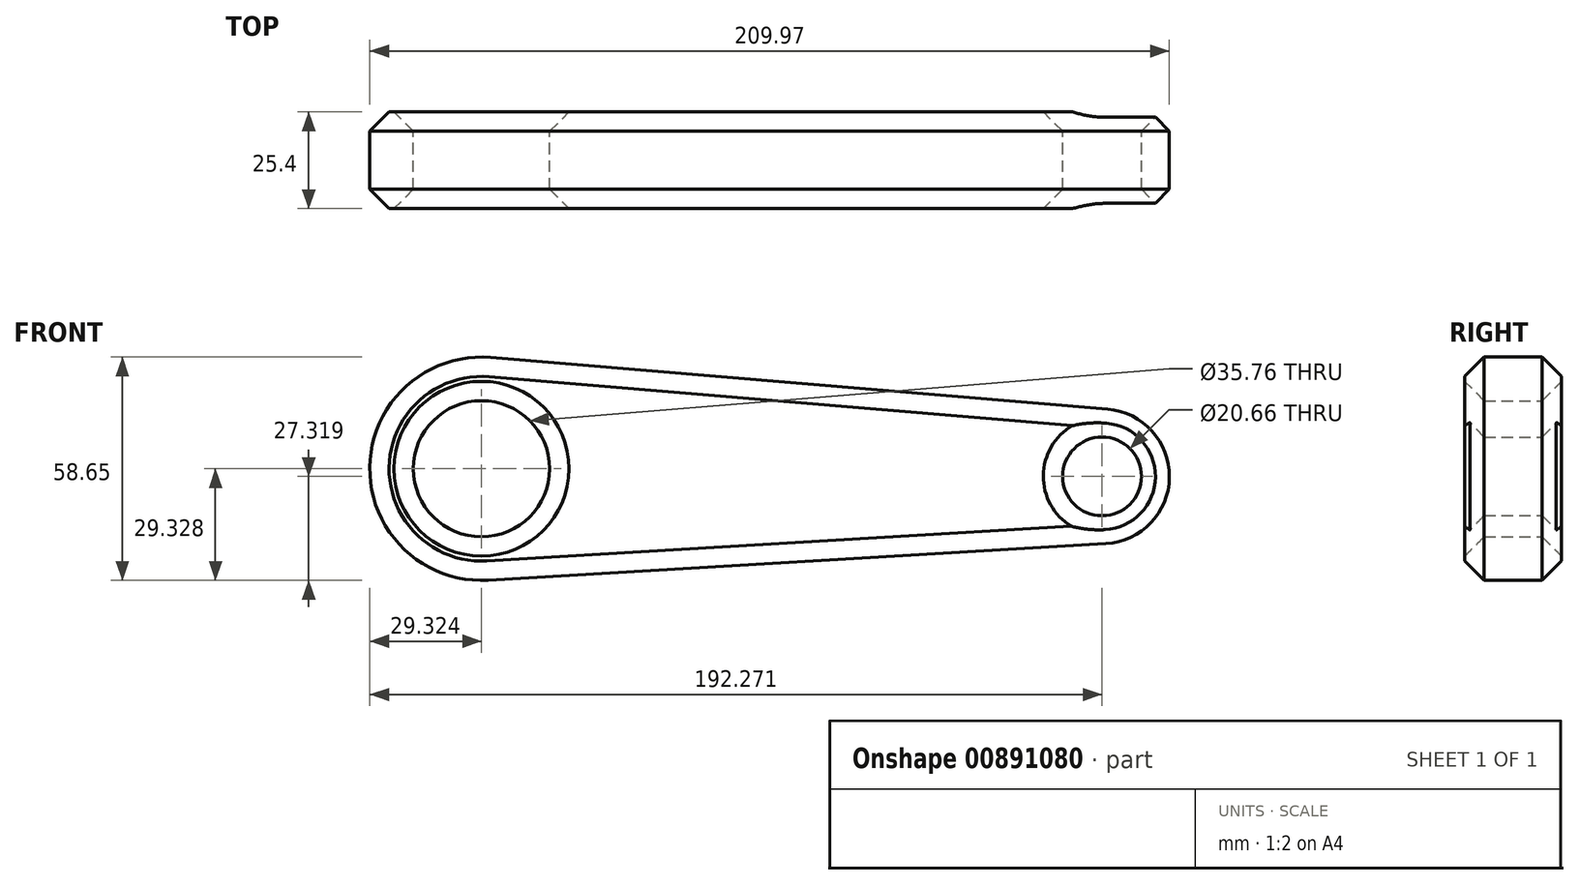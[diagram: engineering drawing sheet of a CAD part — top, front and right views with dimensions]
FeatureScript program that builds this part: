
annotation { "Feature Type Name" : "Feature", "Feature Type Description" : "" }
export const myFeature = defineFeature(function(context is Context, id is Id, definition is map)
    precondition{}
    {
        {
            var Q0;
            Q0=qCreatedBy(makeId("Front.planeOp"),FACE);
            var sketch = newSketch(context, id + "F0", { "sketchPlane" : qUnion([Q0])});
            skCircle(sketch, "E0", {"center": v(-130.06, 19.3) * mm, "radius": 29.33 * mm});
            skCircle(sketch, "E1", {"center": v(32.9, 17.3) * mm, "radius": 17.7 * mm});
            skLineSegment(sketch, "E2", {"start": v(-127.6, 48.53) * mm, "end": v(34.37, 34.94) * mm});
            skLineSegment(sketch, "E3", {"start": v(-128.32, -9.97) * mm, "end": v(33.94, -0.37) * mm});
            skCircle(sketch, "E4", {"center": v(-130.06, 19.3) * mm, "radius": 17.88 * mm});
            skCircle(sketch, "E5", {"center": v(32.9, 17.3) * mm, "radius": 10.33 * mm});
            skSolve(sketch);
        }
        {
            var Q0;
            Q0 = qSketchRegion(id + "F0", true);
            extrude(context, id + "F1", {"entities" : qUnion([Q0]), "depth" : 25.4 * mm, "offsetDistance" : 25.4 * mm});
        }
        {
            var Q0;
            Q0=makeQuery(id+"F1.opExtrude","CAP_EDGE",EDGE,{"disambiguationData":[OSD([sQuery(id+"F0.wireOp",EDGE,"E2")])],"isStart":false});
            var Q1;
            Q1=makeQuery(id+"F1.opExtrude","CAP_EDGE",EDGE,{"disambiguationData":[OSD([sQuery(id+"F0.wireOp",EDGE,"E0")])],"isStart":false});
            var Q2;
            Q2=makeQuery(id+"F1.opExtrude","CAP_EDGE",EDGE,{"disambiguationData":[OSD([sQuery(id+"F0.wireOp",EDGE,"E3")])],"isStart":false});
            var Q3;
            Q3=makeQuery(id+"F1.opExtrude","CAP_EDGE",EDGE,{"disambiguationData":[OSD([sQuery(id+"F0.wireOp",EDGE,"E1")])],"isStart":false});
            var Q4;
            Q4=makeQuery(id+"F1.opExtrude","CAP_EDGE",EDGE,{"disambiguationData":[OSD([sQuery(id+"F0.wireOp",EDGE,"E2")])],"isStart":true});
            var Q5;
            Q5=makeQuery(id+"F1.opExtrude","CAP_EDGE",EDGE,{"disambiguationData":[OSD([sQuery(id+"F0.wireOp",EDGE,"E0")])],"isStart":true});
            var Q6;
            Q6=makeQuery(id+"F1.opExtrude","CAP_EDGE",EDGE,{"disambiguationData":[OSD([sQuery(id+"F0.wireOp",EDGE,"E3")])],"isStart":true});
            var Q7;
            Q7=makeQuery(id+"F1.opExtrude","CAP_EDGE",EDGE,{"disambiguationData":[OSD([sQuery(id+"F0.wireOp",EDGE,"E1")])],"isStart":true});
            var Q8;
            Q8=makeQuery(id+"F1.opExtrude","CAP_EDGE",EDGE,{"disambiguationData":[OSD([sQuery(id+"F0.wireOp",EDGE,"E4")])],"isStart":true});
            var Q9;
            Q9=makeQuery(id+"F1.opExtrude","CAP_EDGE",EDGE,{"disambiguationData":[OSD([sQuery(id+"F0.wireOp",EDGE,"E4")])],"isStart":false});
            var Q10;
            Q10=makeQuery(id+"F1.opExtrude","CAP_EDGE",EDGE,{"disambiguationData":[OSD([sQuery(id+"F0.wireOp",EDGE,"E5")])],"isStart":false});
            var Q11;
            Q11=makeQuery(id+"F1.opExtrude","CAP_EDGE",EDGE,{"disambiguationData":[OSD([sQuery(id+"F0.wireOp",EDGE,"E5")])],"isStart":true});
            chamfer(context, id + "F2", {"entities" : qUnion([Q0, Q1, Q2, Q3, Q4, Q5, Q6, Q7, Q8, Q9, Q10, Q11]), "width" : 5.08 * mm, "tangentPropagation" : true});
        }
    });
